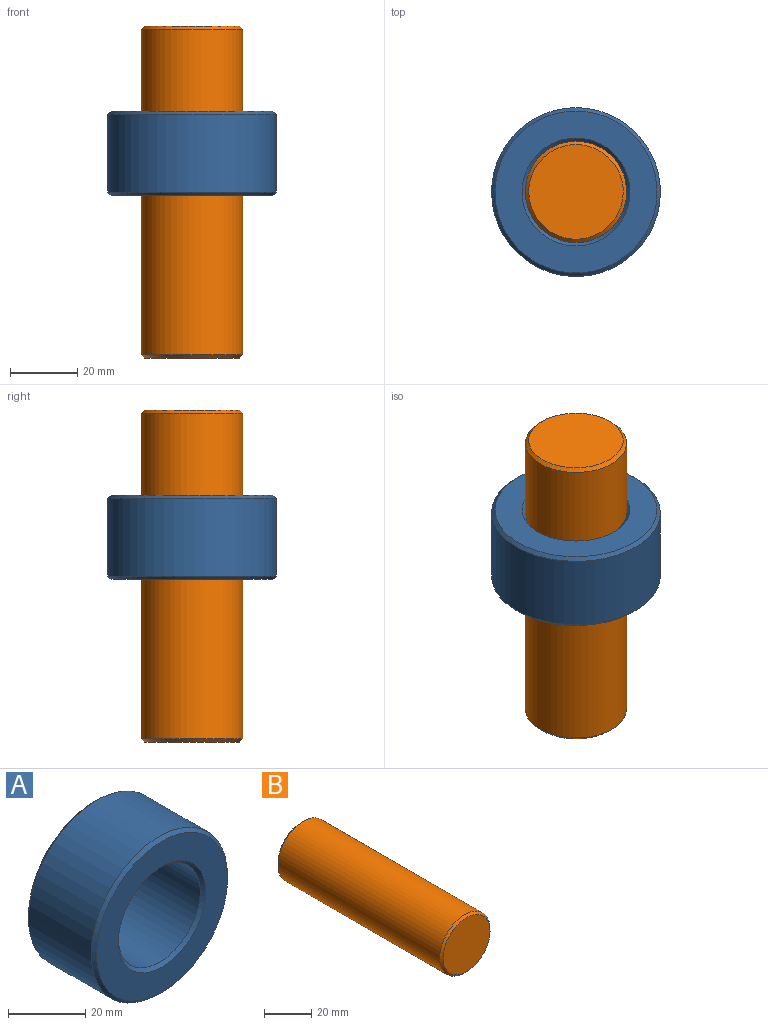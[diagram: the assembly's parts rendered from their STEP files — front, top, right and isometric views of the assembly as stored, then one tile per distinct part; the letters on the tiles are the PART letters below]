
ASSEMBLY  parts=2 mates=1
PART A: 8 faces, bbox 50x25x50 mm
  f0: cylinder r=15mm len=30mm, axis (0,1,0), area 2167.7mm2, adj f6,f7
  f1: cylinder r=25mm len=50mm, axis (0,1,0), area 3612.8mm2, adj f4,f5
  f2: plane 48x48mm, normal (0,-1,0), area 1005.3mm2, adj f4,f7
  f3: plane 48x48mm, normal (0,1,0), area 1005.3mm2, adj f5,f6
  f4: cone r=24mm half-angle=45deg, axis (0,1,0), area 217.7mm2, adj f1,f2
  f5: cone r=25mm half-angle=45deg, axis (0,-1,0), area 217.7mm2, adj f1,f3
  f6: cone r=16mm half-angle=45deg, axis (0,1,0), area 137.7mm2, adj f0,f3
  f7: cone r=15mm half-angle=45deg, axis (0,-1,0), area 137.7mm2, adj f0,f2
PART B: 5 faces, bbox 30x98.4x30 mm
  f0: cylinder r=15mm len=96.4mm, axis (0,-1,0), area 9085.5mm2, adj f3,f4
  f1: plane 28x28mm, normal (0,1,0), area 615.8mm2, adj f3
  f2: plane 28x28mm, normal (0,-1,0), area 615.8mm2, adj f4
  f3: cone r=15mm half-angle=45deg, axis (0,-1,0), area 128.8mm2, adj f0,f1
  f4: cone r=14mm half-angle=45deg, axis (0,1,0), area 128.8mm2, adj f0,f2
PLACE A rot(axis=(1,0,0),90deg) t=(36.56,33.63,24)mm
PLACE B rot(axis=(-1,0,0),90deg) t=(36.56,-33.63,0.8)mm
MATE fastened B.f0 <-> A.f0  axis (0,0,1) through (0,0,0)mm
